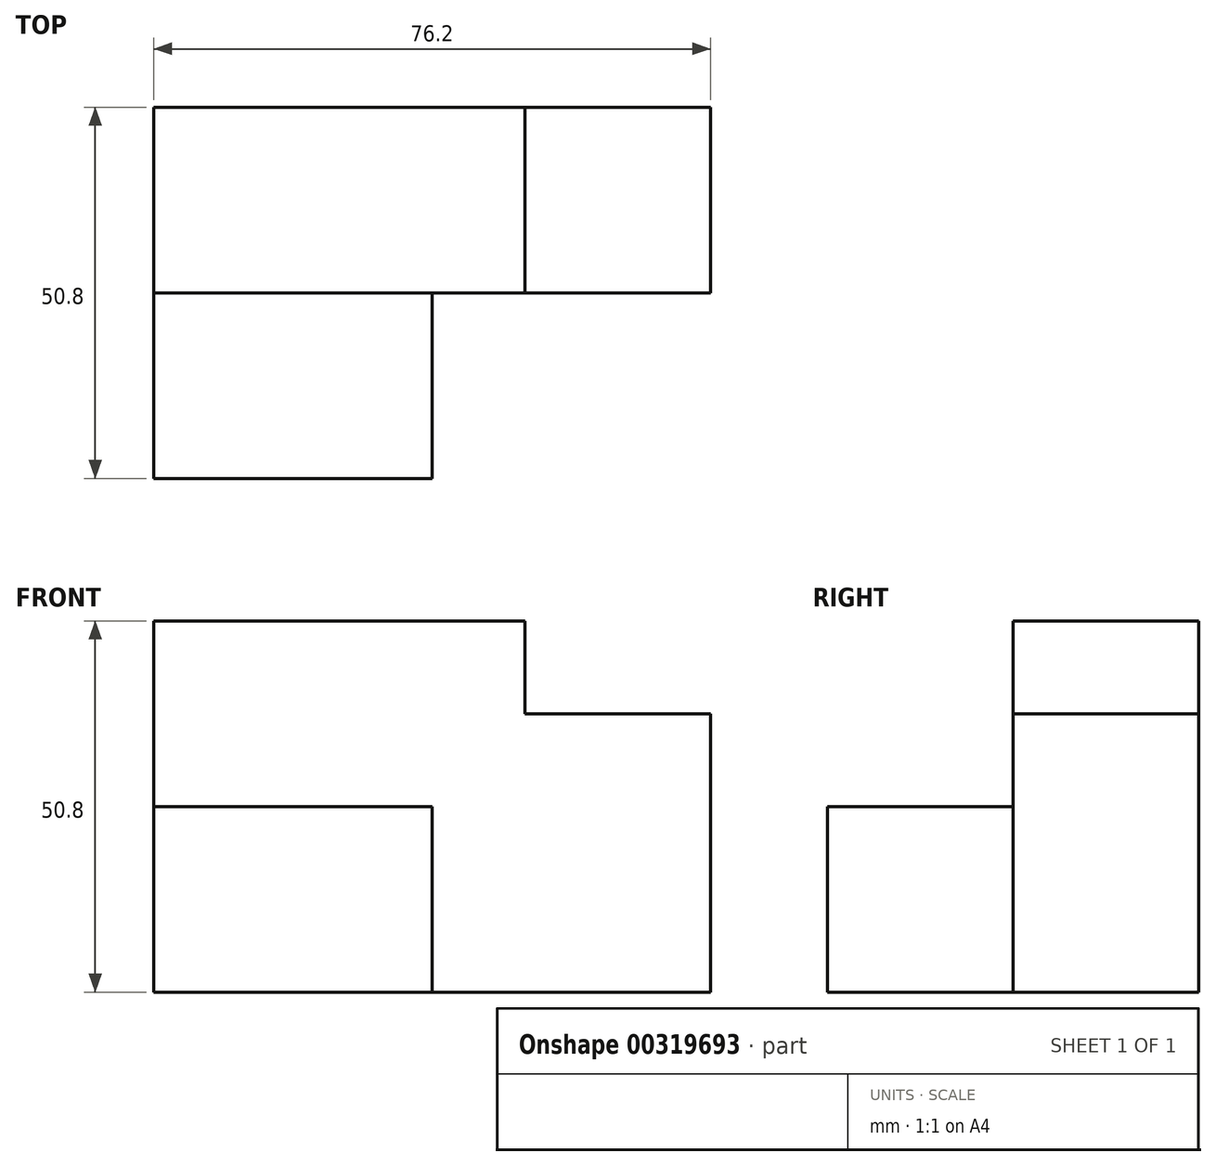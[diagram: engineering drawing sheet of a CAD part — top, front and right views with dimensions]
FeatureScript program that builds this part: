
annotation { "Feature Type Name" : "Feature", "Feature Type Description" : "" }
export const myFeature = defineFeature(function(context is Context, id is Id, definition is map)
    precondition{}
    {
        {
            var Q0;
            Q0=qCreatedBy(makeId("Front.planeOp"),FACE);
            var sketch = newSketch(context, id + "F0", { "sketchPlane" : qUnion([Q0])});
            skLineSegment(sketch, "E0", {"start": v(-48.78, 42.37) * mm, "end": v(-48.78, -8.43) * mm});
            skLineSegment(sketch, "E1", {"start": v(-48.78, 42.37) * mm, "end": v(2.02, 42.37) * mm});
            skLineSegment(sketch, "E2", {"start": v(2.02, 42.37) * mm, "end": v(2.02, 29.67) * mm});
            skLineSegment(sketch, "E3", {"start": v(2.02, 29.67) * mm, "end": v(27.42, 29.67) * mm});
            skLineSegment(sketch, "E4", {"start": v(-48.78, -8.43) * mm, "end": v(27.42, -8.43) * mm});
            skLineSegment(sketch, "E5", {"start": v(27.42, -8.43) * mm, "end": v(27.42, 29.67) * mm});
            skSolve(sketch);
        }
        {
            var Q0;
            Q0=makeQuery(id+"F0.imprint","IMPRINT",FACE,{"disambiguationData":[TD([[makeQuery(id+"F0.imprint","IMPRINT",EDGE,{"derivedFrom":sQuery(id+"F0.wireOp",EDGE,"E0")}),1.0]])]});
            extrude(context, id + "F1", {"entities" : qUnion([Q0]), "oppositeDirection" : true, "depth" : 25.4 * mm});
        }
        {
            var Q0;
            Q0=makeQuery(id+"F1.opExtrude","CAP_FACE",FACE,{"disambiguationData":[OSD([sQuery(id+"F0.wireOp",EDGE,"E0"),sQuery(id+"F0.wireOp",EDGE,"E1"),sQuery(id+"F0.wireOp",EDGE,"E2"),sQuery(id+"F0.wireOp",EDGE,"E3"),sQuery(id+"F0.wireOp",EDGE,"E4"),sQuery(id+"F0.wireOp",EDGE,"E5")])],"isStart":true});
            var sketch = newSketch(context, id + "F2", { "sketchPlane" : qUnion([Q0])});
            skLineSegment(sketch, "E6", {"start": v(-48.78, -8.43) * mm, "end": v(-10.68, -8.43) * mm});
            skLineSegment(sketch, "E7", {"start": v(-10.68, -8.43) * mm, "end": v(-10.68, 16.97) * mm});
            skLineSegment(sketch, "E8", {"start": v(-10.68, 16.97) * mm, "end": v(-48.78, 16.97) * mm});
            skSolve(sketch);
        }
        {
            var Q0;
            {var subQ0=sQuery(id+"F2.wireOp",EDGE,"E6");Q0=makeQuery(id+"F2.imprint","IMPRINT",FACE,{"disambiguationData":[TD([[makeQuery(id+"F2.imprint","IMPRINT",EDGE,{"derivedFrom":subQ0}),1.0]])]});}
            extrude(context, id + "F3", {"entities" : qUnion([Q0]), "operationType" : NewBodyOperationType.ADD, "depth" : 25.4 * mm});
        }
    });
